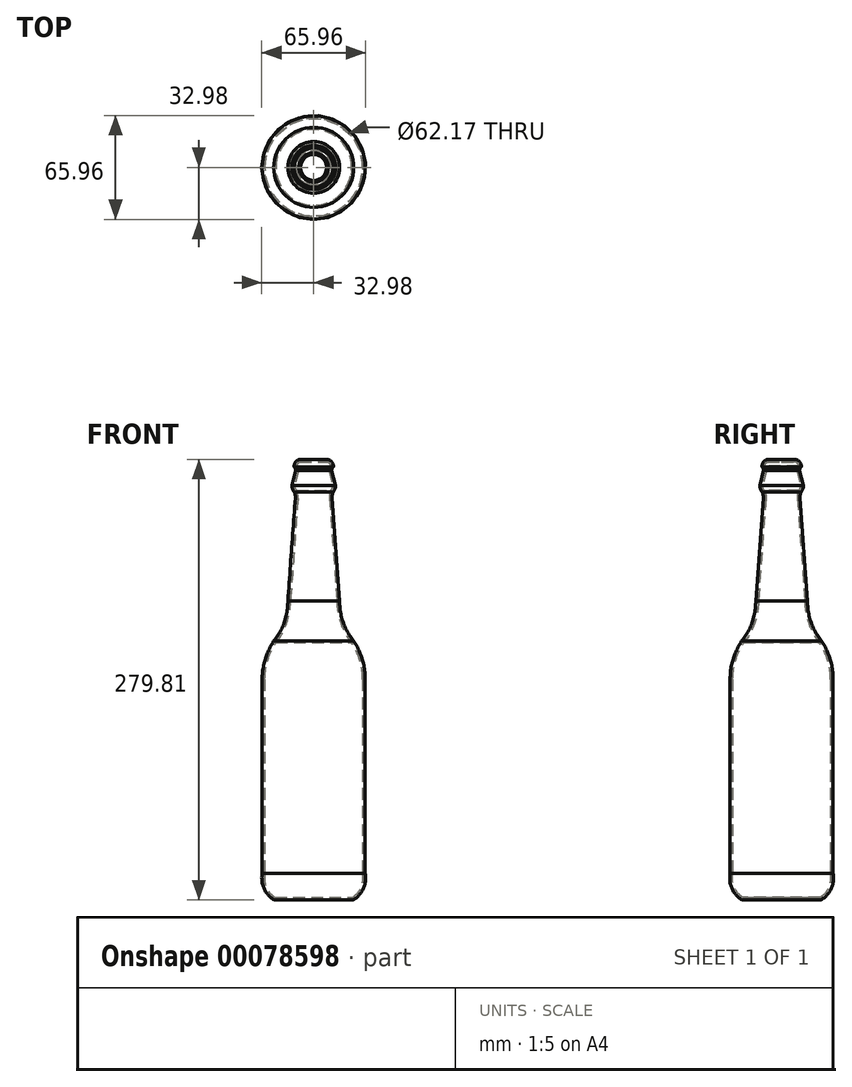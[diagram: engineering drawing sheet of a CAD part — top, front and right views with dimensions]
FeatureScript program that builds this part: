
annotation { "Feature Type Name" : "Feature", "Feature Type Description" : "" }
export const myFeature = defineFeature(function(context is Context, id is Id, definition is map)
    precondition{}
    {
        {
            var Q0;
            Q0=qCreatedBy(makeId("Front.planeOp"),FACE);
            var sketch = newSketch(context, id + "F0", { "sketchPlane" : qUnion([Q0])});
            skLineSegment(sketch, "E0", {"start": v(0, 0) * mm, "end": v(-24.96, 0) * mm});
            skArc(sketch, "E1", {"start": v(-32.72, 16.77) * mm, "mid": v(-31.5, 7.16) * mm, "end": v(-24.96, 0) * mm});
            skLineSegment(sketch, "E2", {"start": v(-32.72, 16.77) * mm, "end": v(-32.72, 140.15) * mm});
            skArc(sketch, "E3", {"start": v(-25.39, 164.41) * mm, "mid": v(-30.85, 152.82) * mm, "end": v(-32.72, 140.15) * mm});
            skArc(sketch, "E4", {"start": v(-25.39, 164.41) * mm, "mid": v(-18.66, 176.43) * mm, "end": v(-16.45, 190.03) * mm});
            skLineSegment(sketch, "E5", {"start": v(-16.45, 190.03) * mm, "end": v(-11.68, 255.25) * mm});
            skArc(sketch, "E6", {"start": v(-11.68, 255.25) * mm, "mid": v(-11.77, 257.24) * mm, "end": v(-12.31, 259.15) * mm});
            skArc(sketch, "E7", {"start": v(-13.9, 263.3) * mm, "mid": v(-13.47, 261.09) * mm, "end": v(-12.31, 259.15) * mm});
            skLineSegment(sketch, "E8", {"start": v(-13.9, 263.3) * mm, "end": v(-11.4, 272.86) * mm});
            skArc(sketch, "E9", {"start": v(-11.4, 272.86) * mm, "mid": v(-11.72, 274.1) * mm, "end": v(-12.52, 275.1) * mm});
            skArc(sketch, "E10", {"start": v(-9.28, 279.8) * mm, "mid": v(-11.69, 278) * mm, "end": v(-12.52, 275.1) * mm});
            skArc(sketch, "E11.0", {"start": v(-8.77, 278.25) * mm, "mid": v(-10.17, 277.3) * mm, "end": v(-10.86, 275.75) * mm});
            skArc(sketch, "E11.1", {"start": v(-24.07, 163.44) * mm, "mid": v(-29.3, 152.31) * mm, "end": v(-31.09, 140.15) * mm});
            skLineSegment(sketch, "E11.2", {"start": v(-31.09, 16.62) * mm, "end": v(-31.09, 140.15) * mm});
            skArc(sketch, "E11.3", {"start": v(-31.09, 16.62) * mm, "mid": v(-30.13, 8.1) * mm, "end": v(-24.5, 1.63) * mm});
            skLineSegment(sketch, "E11.4", {"start": v(0, 1.63) * mm, "end": v(-24.5, 1.63) * mm});
            skArc(sketch, "E11.5", {"start": v(-24.07, 163.44) * mm, "mid": v(-17.12, 175.9) * mm, "end": v(-14.82, 189.98) * mm});
            skLineSegment(sketch, "E11.6", {"start": v(-14.82, 189.98) * mm, "end": v(-10.05, 255.13) * mm});
            skArc(sketch, "E11.7", {"start": v(-10.05, 255.13) * mm, "mid": v(-10.18, 257.64) * mm, "end": v(-10.92, 260.04) * mm});
            skArc(sketch, "E11.8", {"start": v(-12.26, 263.12) * mm, "mid": v(-11.86, 261.47) * mm, "end": v(-10.92, 260.04) * mm});
            skLineSegment(sketch, "E11.9", {"start": v(-12.26, 263.12) * mm, "end": v(-9.78, 272.64) * mm});
            skArc(sketch, "E11.10", {"start": v(-9.78, 272.64) * mm, "mid": v(-10.03, 274.3) * mm, "end": v(-10.86, 275.75) * mm});
            skArc(sketch, "E12", {"start": v(-8.77, 278.25) * mm, "mid": v(-8.35, 279.25) * mm, "end": v(-9.28, 279.8) * mm});
            skLineSegment(sketch, "E13", {"start": v(0, 1.63) * mm, "end": v(0, 0) * mm});
            skLineSegment(sketch, "E14", {"start": v(0, -36.89) * mm, "end": v(0, 350.1) * mm, "construction": true});
            skSolve(sketch);
        }
        {
            var Q0;
            Q0 = qSketchRegion(id + "F0", true);
            var Q1;
            Q1=sQuery(id+"F0.wireOp",EDGE,"E14");
            revolve(context, id + "F1", {"entities" : qUnion([Q0]), "axis" : qUnion([Q1]), "revolveType" : RevolveType.FULL});
        }
    });
